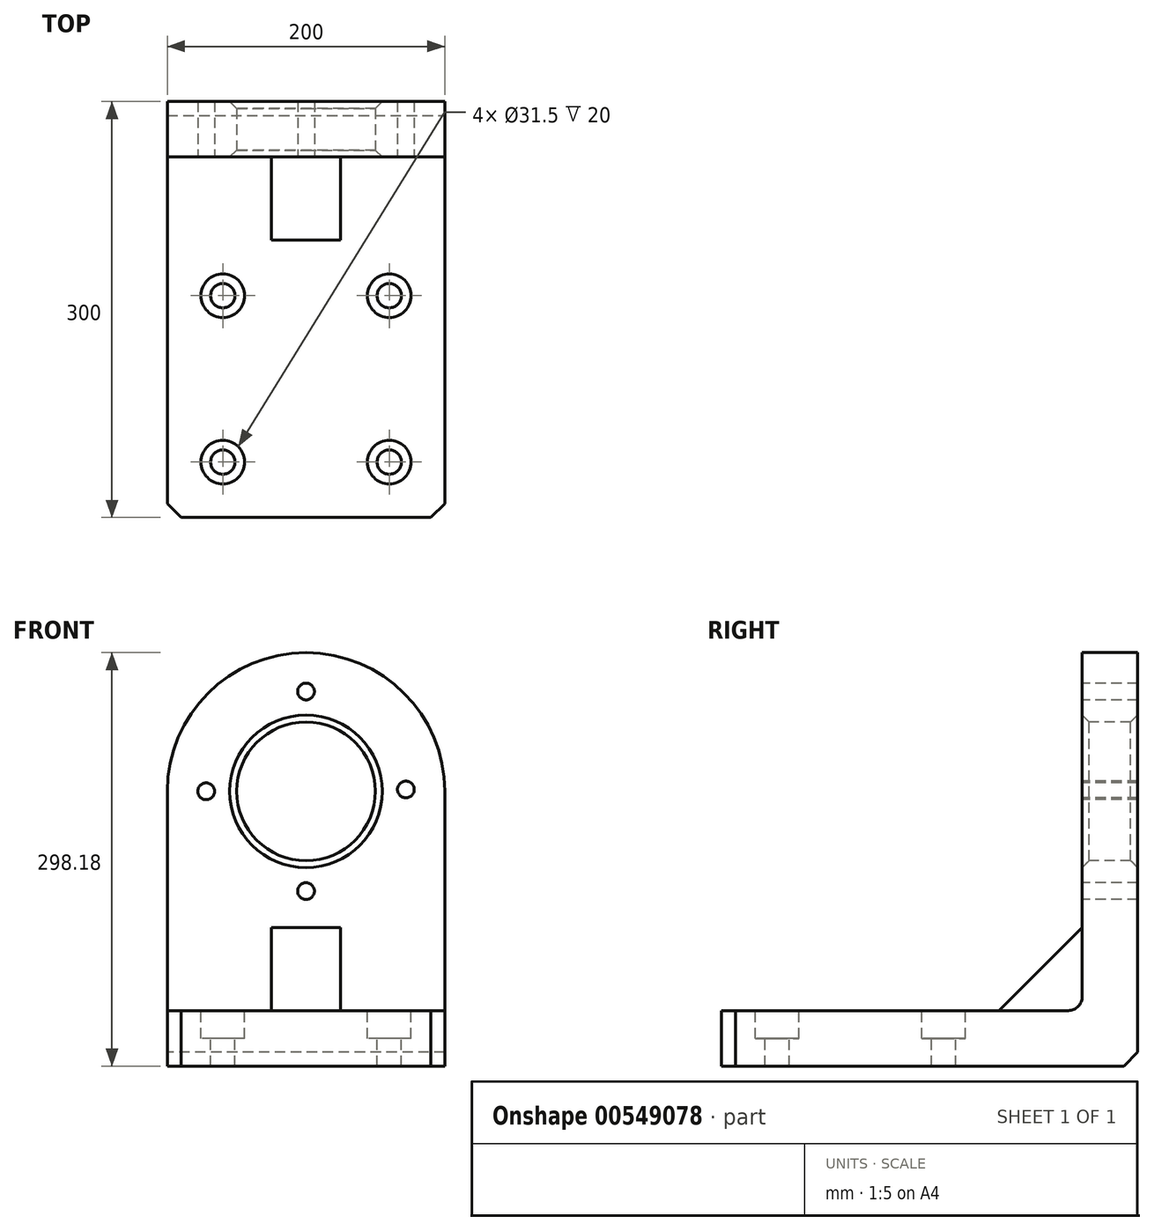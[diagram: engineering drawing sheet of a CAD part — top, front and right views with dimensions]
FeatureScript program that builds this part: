
annotation { "Feature Type Name" : "Feature", "Feature Type Description" : "" }
export const myFeature = defineFeature(function(context is Context, id is Id, definition is map)
    precondition{}
    {
        {
            var Q0;
            Q0=qCreatedBy(makeId("Front.planeOp"),FACE);
            var sketch = newSketch(context, id + "F0", { "sketchPlane" : qUnion([Q0])});
            skLineSegment(sketch, "E0.bottom", {"start": v(0, -40) * mm, "end": v(-100, -40) * mm});
            skLineSegment(sketch, "E0.top", {"start": v(0, 158.18) * mm, "end": v(-100, 158.18) * mm, "construction": true});
            skLineSegment(sketch, "E0.right", {"start": v(-100, -40) * mm, "end": v(-100, 158.18) * mm});
            skLineSegment(sketch, "E1.MirrorCS", {"start": v(100, 0) * mm, "end": v(100, 160) * mm});
            skLineSegment(sketch, "E2.MirrorCS", {"start": v(0, 158.18) * mm, "end": v(100, 160) * mm, "construction": true});
            skLineSegment(sketch, "E3", {"start": v(0, 158.18) * mm, "end": v(0, 360.63) * mm, "construction": true});
            skLineSegment(sketch, "E4", {"start": v(0, -40) * mm, "end": v(0, -157.4) * mm, "construction": true});
            skCircle(sketch, "E5", {"center": v(0, 158.18) * mm, "radius": 100 * mm});
            skCircle(sketch, "E6", {"center": v(0, 158.18) * mm, "radius": 50 * mm});
            skCircle(sketch, "E7", {"center": v(0, 158.18) * mm, "radius": 72 * mm, "construction": true});
            skPoint(sketch, "E8", {"position": v(0, 230.18) * mm});
            skPoint(sketch, "E9", {"position": v(-72, 158.18) * mm});
            skPoint(sketch, "E10", {"position": v(71.99, 159.49) * mm});
            skPoint(sketch, "E11", {"position": v(0, 86.18) * mm});
            skLineSegment(sketch, "E12.bottom", {"start": v(-100, -40) * mm, "end": v(100, -40) * mm});
            skLineSegment(sketch, "E12.top", {"start": v(-100, 0) * mm, "end": v(100, 0) * mm});
            skLineSegment(sketch, "E12.left", {"start": v(-100, -40) * mm, "end": v(-100, 0) * mm});
            skLineSegment(sketch, "E12.right", {"start": v(100, -40) * mm, "end": v(100, 0) * mm});
            skLineSegment(sketch, "E13.bottom", {"start": v(0, 0) * mm, "end": v(-25, 0) * mm, "construction": true});
            skLineSegment(sketch, "E13.right", {"start": v(-25, 0) * mm, "end": v(-25, 60) * mm, "construction": true});
            skLineSegment(sketch, "E14.MirrorCS", {"start": v(25, 0) * mm, "end": v(25, 60) * mm, "construction": true});
            skLineSegment(sketch, "E15", {"start": v(0, 158.18) * mm, "end": v(0, -40) * mm, "construction": true});
            skPoint(sketch, "E16", {"position": v(25, 0) * mm});
            skLineSegment(sketch, "E17", {"start": v(-25, 60) * mm, "end": v(25, 60) * mm, "construction": true});
            skPoint(sketch, "E18", {"position": v(-25, 0) * mm});
            skSolve(sketch);
        }
        {
            var Q0;
            {var subQ1=sQuery(id+"F0.wireOp",EDGE,"E0.right");Q0=makeQuery(id+"F0.imprint","IMPRINT",FACE,{"disambiguationData":[TD([[makeQuery(id+"F0.imprint","IMPRINT",EDGE,{"derivedFrom":subQ1}),-1.0]])]});}
            var Q1;
            {var subQ1=sQuery(id+"F0.wireOp",EDGE,"E1.MirrorCS");Q1=makeQuery(id+"F0.imprint","IMPRINT",FACE,{"disambiguationData":[TD([[makeQuery(id+"F0.imprint","IMPRINT",EDGE,{"derivedFrom":subQ1}),1.0]])]});}
            var Q2;
            Q2=makeQuery(id+"F0.imprint","IMPRINT",FACE,{"disambiguationData":[TD([[makeQuery(id+"F0.imprint","IMPRINT",EDGE,{"derivedFrom":sQuery(id+"F0.wireOp",EDGE,"E12.bottom")}),1.0]])]});
            var Q3;
            Q3=makeQuery(id+"F0.imprint","IMPRINT",FACE,{"disambiguationData":[TD([[makeQuery(id+"F0.imprint","IMPRINT",EDGE,{"derivedFrom":sQuery(id+"F0.wireOp",EDGE,"E13.bottom")}),-1.0]])]});
            var Q4;
            {var subQ0=sQuery(id+"F0.wireOp",EDGE,"E13.left");Q4=makeQuery(id+"F0.imprint","IMPRINT",FACE,{"disambiguationData":[TD([[makeQuery(id+"F0.imprint","IMPRINT",EDGE,{"derivedFrom":subQ0}),-1.0]])]});}
            var Q5;
            Q5=makeQuery(id+"F0.imprint","IMPRINT",FACE,{"disambiguationData":[TD([[makeQuery(id+"F0.imprint","IMPRINT",EDGE,{"derivedFrom":sQuery(id+"F0.wireOp",EDGE,"E6")}),-1.0]])]});
            var Q6;
            {var subQ1=sQuery(id+"F0.wireOp",EDGE,"E12.left");Q6=makeQuery(id+"F0.imprint","IMPRINT",FACE,{"disambiguationData":[TD([[makeQuery(id+"F0.imprint","IMPRINT",EDGE,{"derivedFrom":subQ1}),-1.0]])]});}
            extrude(context, id + "F1", {"entities" : qUnion([Q0, Q1, Q2, Q3, Q4, Q5, Q6]), "oppositeDirection" : true, "depth" : 40 * mm, "offsetDistance" : 25 * mm});
        }
        {
            var Q0;
            Q0=sQuery(id+"F0.wireOp",VERTEX,"E9");
            var Q1;
            Q1=sQuery(id+"F0.wireOp",VERTEX,"E8");
            var Q2;
            Q2=sQuery(id+"F0.wireOp",VERTEX,"E10");
            var Q3;
            Q3=sQuery(id+"F0.wireOp",VERTEX,"E11");
            var Q4;
            Q4=makeQuery(id+"F1.opExtrude","SWEPT_BODY",BODY,{"disambiguationData":[OSD([sQuery(id+"F0.wireOp",EDGE,"E0.right"),sQuery(id+"F0.wireOp",EDGE,"E1.MirrorCS"),sQuery(id+"F0.wireOp",EDGE,"E5"),sQuery(id+"F0.wireOp",EDGE,"E6"),sQuery(id+"F0.wireOp",EDGE,"E12.bottom"),sQuery(id+"F0.wireOp",EDGE,"E12.left"),sQuery(id+"F0.wireOp",EDGE,"E12.right")])]});
            hole(context, id + "F2", {"style" : HoleStyle.SIMPLE, "endStyle" : HoleEndStyle.THROUGH, "standardTappedOrClearance" : lookupTablePath({ "standard" : "ISO", "engagement" : "75%", "pitch" : "2 mm", "size" : "M14", "type" : "Tapped" }), "standardBlindInLast" : lookupTablePath({ "standard" : "ISO", "engagement" : "75%", "pitch" : "2 mm", "size" : "M14", "type" : "Tapped" }), "holeDiameter" : 12.1 * mm, "showTappedDepth" : true, "isTappedThrough" : true, "tappedDepth" : 12 * mm, "tapClearance" : 3, "locations" : qUnion([Q0, Q1, Q2, Q3]), "scope" : qUnion([Q4]), "majorDiameter" : 14 * mm});
        }
        {
            var Q0;
            Q0=qCreatedBy(makeId("Top.planeOp"),FACE);
            var sketch = newSketch(context, id + "F3", { "sketchPlane" : qUnion([Q0])});
            skLineSegment(sketch, "E19.bottom", {"start": v(-100, 40) * mm, "end": v(100, 40) * mm});
            skLineSegment(sketch, "E19.top", {"start": v(-100, -260) * mm, "end": v(100, -260) * mm});
            skLineSegment(sketch, "E19.left", {"start": v(-100, 40) * mm, "end": v(-100, -260) * mm});
            skLineSegment(sketch, "E19.right", {"start": v(100, 40) * mm, "end": v(100, -260) * mm});
            skLineSegment(sketch, "E20.top", {"start": v(-100, -220) * mm, "end": v(100, -220) * mm, "construction": true});
            skLineSegment(sketch, "E20.left", {"start": v(-100, -260) * mm, "end": v(-100, -220) * mm});
            skLineSegment(sketch, "E20.right", {"start": v(100, -260) * mm, "end": v(100, -220) * mm});
            skLineSegment(sketch, "E21", {"start": v(-60, -260) * mm, "end": v(-60, -220) * mm, "construction": true});
            skLineSegment(sketch, "E22.MirrorCS", {"start": v(60, -260) * mm, "end": v(60, -220) * mm, "construction": true});
            skLineSegment(sketch, "E23", {"start": v(-60, -220) * mm, "end": v(-60, 40) * mm, "construction": true});
            skLineSegment(sketch, "E24.MirrorCS", {"start": v(60, -220) * mm, "end": v(60, 40) * mm, "construction": true});
            skPoint(sketch, "E25", {"position": v(-60, -220) * mm});
            skPoint(sketch, "E26", {"position": v(60, -220) * mm});
            skPoint(sketch, "E27", {"position": v(-60, -100) * mm});
            skLineSegment(sketch, "E28", {"start": v(-60, -100) * mm, "end": v(100, -100) * mm, "construction": true});
            skLineSegment(sketch, "E29", {"start": v(-60, -100) * mm, "end": v(-100, -100) * mm, "construction": true});
            skPoint(sketch, "E30", {"position": v(60, -100) * mm});
            skLineSegment(sketch, "E31", {"start": v(-25, 0) * mm, "end": v(-25, -260) * mm, "construction": true});
            skLineSegment(sketch, "E32.MirrorCS", {"start": v(25, 0) * mm, "end": v(25, -260) * mm, "construction": true});
            skLineSegment(sketch, "E33", {"start": v(25, -60) * mm, "end": v(-25, -60) * mm});
            skLineSegment(sketch, "E34", {"start": v(-25, -60) * mm, "end": v(-25, 40) * mm});
            skLineSegment(sketch, "E35", {"start": v(25, -60) * mm, "end": v(25, 40) * mm});
            skSolve(sketch);
        }
        {
            var Q0;
            Q0 = qSketchRegion(id + "F3", true);
            extrude(context, id + "F4", {"entities" : qUnion([Q0]), "operationType" : NewBodyOperationType.ADD, "oppositeDirection" : true, "depth" : 40 * mm, "offsetDistance" : 25 * mm});
        }
        {
            var Q0;
            Q0=sQuery(id+"F3.wireOp",VERTEX,"E27");
            var Q1;
            Q1=sQuery(id+"F3.wireOp",VERTEX,"E30");
            var Q2;
            Q2=sQuery(id+"F3.wireOp",VERTEX,"E26");
            var Q3;
            Q3=sQuery(id+"F3.wireOp",VERTEX,"E25");
            var Q4;
            Q4=makeQuery(id+"F1.opExtrude","SWEPT_BODY",BODY,{"disambiguationData":[OSD([sQuery(id+"F0.wireOp",EDGE,"E0.right"),sQuery(id+"F0.wireOp",EDGE,"E1.MirrorCS"),sQuery(id+"F0.wireOp",EDGE,"E5"),sQuery(id+"F0.wireOp",EDGE,"E6"),sQuery(id+"F0.wireOp",EDGE,"E12.bottom"),sQuery(id+"F0.wireOp",EDGE,"E12.left"),sQuery(id+"F0.wireOp",EDGE,"E12.right")])]});
            hole(context, id + "F5", {"style" : HoleStyle.C_BORE, "endStyle" : HoleEndStyle.THROUGH, "holeDiameter" : 17.5 * mm, "cBoreDiameter" : 31.5 * mm, "cBoreDepth" : 20 * mm, "isTappedThrough" : true, "tappedDepth" : 12 * mm, "tapClearance" : 3, "locations" : qUnion([Q0, Q1, Q2, Q3]), "scope" : qUnion([Q4])});
        }
        {
            var Q0;
            Q0=qCreatedBy(makeId("Right.planeOp"),FACE);
            var sketch = newSketch(context, id + "F6", { "sketchPlane" : qUnion([Q0])});
            skLineSegment(sketch, "E36.bottom", {"start": v(0, 0) * mm, "end": v(-60, 0) * mm});
            skLineSegment(sketch, "E36.top", {"start": v(0, 60) * mm, "end": v(-60, 60) * mm, "construction": true});
            skLineSegment(sketch, "E36.left", {"start": v(0, 0) * mm, "end": v(0, 60) * mm});
            skLineSegment(sketch, "E36.right", {"start": v(-60, 0) * mm, "end": v(-60, 60) * mm, "construction": true});
            skLineSegment(sketch, "E37", {"start": v(-60, 0) * mm, "end": v(0, 60) * mm});
            skLineSegment(sketch, "E38", {"start": v(0, 0) * mm, "end": v(20, 0) * mm});
            skLineSegment(sketch, "E39", {"start": v(20, 0) * mm, "end": v(20, 160) * mm});
            skPoint(sketch, "E40", {"position": v(20, 160) * mm});
            skSolve(sketch);
        }
        {
            var Q0;
            Q0 = qSketchRegion(id + "F6", true);
            extrude(context, id + "F7", {"entities" : qUnion([Q0]), "operationType" : NewBodyOperationType.ADD, "endBound" : BoundingType.SYMMETRIC, "depth" : 50 * mm, "offsetDistance" : 25 * mm});
        }
        {
            var Q0;
            Q0=makeQuery(id+"F1.opExtrude","CAP_EDGE",EDGE,{"disambiguationData":[OSD([sQuery(id+"F0.wireOp",EDGE,"E6")])],"isStart":true});
            var Q1;
            Q1=makeQuery(id+"F1.opExtrude","CAP_EDGE",EDGE,{"disambiguationData":[OSD([sQuery(id+"F0.wireOp",EDGE,"E6")])],"isStart":false});
            chamfer(context, id + "F8", {"entities" : qUnion([Q0, Q1]), "width" : 5 * mm, "tangentPropagation" : true});
        }
        {
            var Q0;
            Q0=makeQuery(id+"F1.opExtrude","CAP_EDGE",EDGE,{"disambiguationData":[OSD([sQuery(id+"F0.wireOp",EDGE,"E12.bottom")])],"isStart":false});
            var Q1;
            Q1=makeQuery(id+"F4.opExtrude","SWEPT_EDGE",EDGE,{"disambiguationData":[OSD([sQuery(id+"F3.wireOp",EDGE,"E19.top"),sQuery(id+"F3.wireOp",EDGE,"E20.left")])]});
            var Q2;
            Q2=makeQuery(id+"F4.opExtrude","SWEPT_EDGE",EDGE,{"disambiguationData":[OSD([sQuery(id+"F3.wireOp",EDGE,"E19.top"),sQuery(id+"F3.wireOp",EDGE,"E20.right")])]});
            chamfer(context, id + "F9", {"entities" : qUnion([Q0, Q1, Q2]), "width" : 10 * mm, "tangentPropagation" : true});
        }
        {
            var Q0;
            {var subQ0=sQuery(id+"F3.wireOp",EDGE,"E20.left");var subQ1=sQuery(id+"F3.wireOp",EDGE,"E19.left");var subQ2=makeQuery(id+"F4.opExtrude","CAP_FACE",FACE,{"disambiguationData":[OSD([sQuery(id+"F3.wireOp",EDGE,"E19.bottom"),subQ1,sQuery(id+"F3.wireOp",EDGE,"E19.right"),sQuery(id+"F3.wireOp",EDGE,"E19.top"),subQ0,sQuery(id+"F3.wireOp",EDGE,"E20.right")])],"isStart":true});var subQ3=sQuery(id+"F0.wireOp",EDGE,"E12.left");var subQ4=sQuery(id+"F0.wireOp",EDGE,"E0.right");var subQ5=makeQuery(id+"F1.opExtrude","CAP_FACE",FACE,{"disambiguationData":[OSD([subQ4,sQuery(id+"F0.wireOp",EDGE,"E1.MirrorCS"),sQuery(id+"F0.wireOp",EDGE,"E5"),sQuery(id+"F0.wireOp",EDGE,"E6"),sQuery(id+"F0.wireOp",EDGE,"E12.bottom"),subQ3,sQuery(id+"F0.wireOp",EDGE,"E12.right")])],"isStart":true});Q0=makeQuery(id+"F7.boolean.opBoolean","SPLIT",EDGE,{"disambiguationData":[TD([makeQuery(id+"F1.opExtrude","SWEPT_FACE",FACE,{"disambiguationData":[OSD([subQ4,subQ3])]})])],"derivedFrom":makeQuery(id+"F4.boolean.opBoolean","INTERSECT",EDGE,{"derivedFrom":[subQ5,subQ2]})});}
            var Q1;
            {var subQ0=sQuery(id+"F3.wireOp",EDGE,"E20.right");var subQ1=sQuery(id+"F3.wireOp",EDGE,"E19.right");var subQ2=makeQuery(id+"F4.opExtrude","CAP_FACE",FACE,{"disambiguationData":[OSD([sQuery(id+"F3.wireOp",EDGE,"E19.bottom"),sQuery(id+"F3.wireOp",EDGE,"E19.left"),subQ1,sQuery(id+"F3.wireOp",EDGE,"E19.top"),sQuery(id+"F3.wireOp",EDGE,"E20.left"),subQ0])],"isStart":true});var subQ3=sQuery(id+"F0.wireOp",EDGE,"E12.right");var subQ4=sQuery(id+"F0.wireOp",EDGE,"E1.MirrorCS");var subQ5=makeQuery(id+"F1.opExtrude","CAP_FACE",FACE,{"disambiguationData":[OSD([sQuery(id+"F0.wireOp",EDGE,"E0.right"),subQ4,sQuery(id+"F0.wireOp",EDGE,"E5"),sQuery(id+"F0.wireOp",EDGE,"E6"),sQuery(id+"F0.wireOp",EDGE,"E12.bottom"),sQuery(id+"F0.wireOp",EDGE,"E12.left"),subQ3])],"isStart":true});Q1=makeQuery(id+"F7.boolean.opBoolean","SPLIT",EDGE,{"disambiguationData":[TD([makeQuery(id+"F1.opExtrude","SWEPT_FACE",FACE,{"disambiguationData":[OSD([subQ4,subQ3])]})])],"derivedFrom":makeQuery(id+"F4.boolean.opBoolean","INTERSECT",EDGE,{"derivedFrom":[subQ5,subQ2]})});}
            fillet(context, id + "F10", {"entities" : qUnion([Q0, Q1]), "radius" : 10 * mm, "tangentPropagation" : true, "allowEdgeOverflow" : false});
        }
    });
